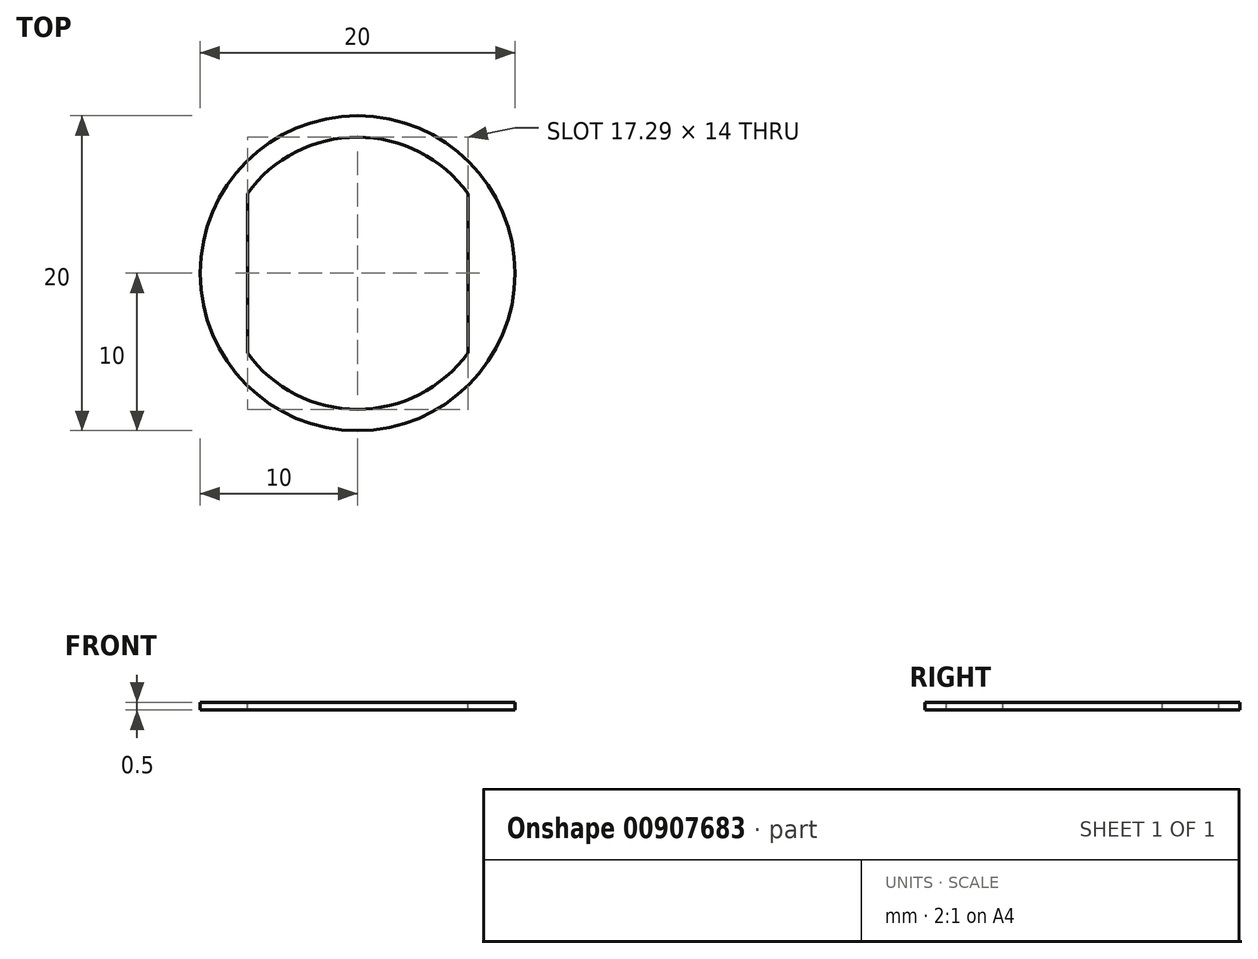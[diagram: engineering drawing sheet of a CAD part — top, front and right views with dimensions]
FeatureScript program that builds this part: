
annotation { "Feature Type Name" : "Feature", "Feature Type Description" : "" }
export const myFeature = defineFeature(function(context is Context, id is Id, definition is map)
    precondition{}
    {
        {
            var Q0;
            Q0=qCreatedBy(makeId("Top.planeOp"),FACE);
            var sketch = newSketch(context, id + "F0", { "sketchPlane" : qUnion([Q0])});
            skCircle(sketch, "E0", {"center": v(0, 0) * mm, "radius": 10 * mm});
            skSolve(sketch);
        }
        {
            var Q0;
            Q0 = qSketchRegion(id + "F0", true);
            extrude(context, id + "F1", {"entities" : qUnion([Q0]), "depth" : .5 * mm, "offsetDistance" : 25 * mm});
        }
        {
            var Q0;
            Q0=makeQuery(id+"F1.opExtrude","CAP_FACE",FACE,{"disambiguationData":[OSD([sQuery(id+"F0.wireOp",EDGE,"E0")])],"isStart":false});
            var sketch = newSketch(context, id + "F2", { "sketchPlane" : qUnion([Q0])});
            skCircle(sketch, "E1", {"center": v(0, 0) * mm, "radius": 8.64 * mm});
            skLineSegment(sketch, "E2", {"start": v(-7, 5.07) * mm, "end": v(-7, -5.07) * mm});
            skLineSegment(sketch, "E3", {"start": v(7, 5.07) * mm, "end": v(7, -5.07) * mm});
            skSolve(sketch);
        }
        {
            var Q0;
            {var subQ0=sQuery(id+"F2.wireOp",EDGE,"E2");Q0=makeQuery(id+"F2.imprint","IMPRINT",FACE,{"disambiguationData":[TD([[makeQuery(id+"F2.imprint","IMPRINT",EDGE,{"derivedFrom":subQ0}),1.0]])]});}
            extrude(context, id + "F3", {"entities" : qUnion([Q0]), "operationType" : NewBodyOperationType.REMOVE, "oppositeDirection" : true, "depth" : 25 * mm, "offsetDistance" : 25 * mm});
        }
    });
